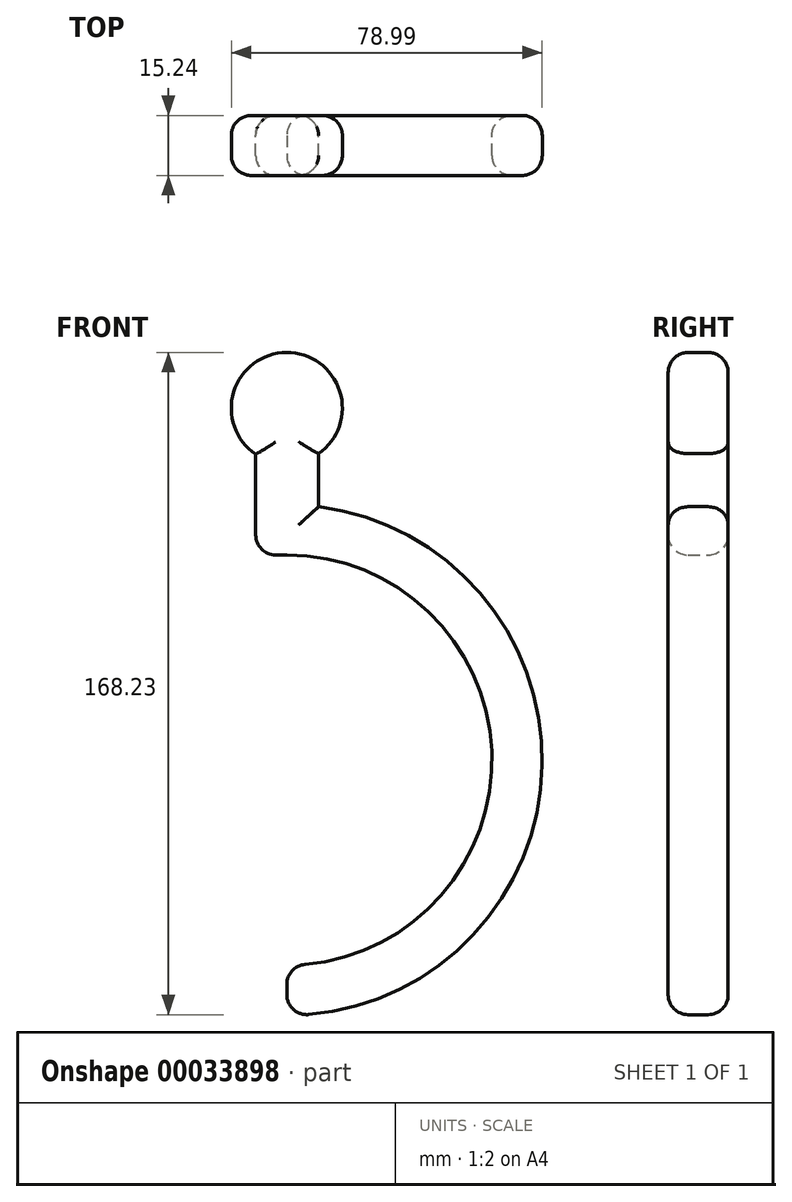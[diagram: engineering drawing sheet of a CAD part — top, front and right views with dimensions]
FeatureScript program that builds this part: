
annotation { "Feature Type Name" : "Feature", "Feature Type Description" : "" }
export const myFeature = defineFeature(function(context is Context, id is Id, definition is map)
    precondition{}
    {
        {
            var Q0;
            Q0=qCreatedBy(makeId("Front.planeOp"),FACE);
            var sketch = newSketch(context, id + "F0", { "sketchPlane" : qUnion([Q0])});
            skArc(sketch, "E0", {"start": v(0, -64.88) * mm, "mid": v(64.88, 0) * mm, "end": v(0, 64.88) * mm});
            skArc(sketch, "E1", {"start": v(0, -52.11) * mm, "mid": v(52.11, 0) * mm, "end": v(0, 52.11) * mm});
            skPoint(sketch, "E2", {"position": v(0, 64.88) * mm});
            skPoint(sketch, "E3", {"position": v(0, 52.11) * mm});
            skPoint(sketch, "E4", {"position": v(0, -52.11) * mm});
            skPoint(sketch, "E5", {"position": v(0, -64.88) * mm});
            skLineSegment(sketch, "E6", {"start": v(0, 64.88) * mm, "end": v(0, 52.11) * mm});
            skLineSegment(sketch, "E7", {"start": v(0, -52.11) * mm, "end": v(0, -64.88) * mm});
            skLineSegment(sketch, "E8.bottom", {"start": v(0, 64.88) * mm, "end": v(-7.9, 64.88) * mm});
            skLineSegment(sketch, "E8.top", {"start": v(0, 89.45) * mm, "end": v(-7.9, 89.45) * mm});
            skLineSegment(sketch, "E8.left", {"start": v(0, 64.88) * mm, "end": v(0, 89.45) * mm});
            skLineSegment(sketch, "E8.right", {"start": v(-7.9, 64.88) * mm, "end": v(-7.9, 89.45) * mm});
            skLineSegment(sketch, "E9.top", {"start": v(0, 52.11) * mm, "end": v(-7.9, 52.11) * mm});
            skLineSegment(sketch, "E9.right", {"start": v(-7.9, 64.88) * mm, "end": v(-7.9, 52.11) * mm});
            skLineSegment(sketch, "E10.bottom", {"start": v(0, 89.45) * mm, "end": v(8.08, 89.45) * mm});
            skLineSegment(sketch, "E10.top", {"start": v(0, 64.38) * mm, "end": v(8.08, 64.38) * mm});
            skLineSegment(sketch, "E10.left", {"start": v(0, 89.45) * mm, "end": v(0, 64.38) * mm});
            skLineSegment(sketch, "E10.right", {"start": v(8.08, 89.45) * mm, "end": v(8.08, 64.38) * mm});
            skCircle(sketch, "E11", {"center": v(0, 89.45) * mm, "radius": 14.11 * mm});
            skSolve(sketch);
        }
        {
            var Q0;
            Q0 = qSketchRegion(id + "F0", true);
            extrude(context, id + "F1", {"entities" : qUnion([Q0]), "depth" : 7.62 * mm, "hasSecondDirection" : true, "secondDirectionOppositeDirection" : true, "secondDirectionDepth" : 7.62 * mm});
        }
        {
            var Q0;
            Q0=makeQuery(id+"F1.opExtrude","CAP_EDGE",EDGE,{"disambiguationData":[OSD([sQuery(id+"F0.wireOp",EDGE,"E0")])],"isStart":false});
            var Q1;
            Q1=makeQuery(id+"F1.opExtrude","CAP_EDGE",EDGE,{"disambiguationData":[OSD([sQuery(id+"F0.wireOp",EDGE,"E0")])],"isStart":true});
            var Q2;
            Q2=makeQuery(id+"F1.opExtrude","CAP_EDGE",EDGE,{"disambiguationData":[OSD([sQuery(id+"F0.wireOp",EDGE,"E10.right")])],"isStart":false});
            var Q3;
            Q3=makeQuery(id+"F1.opExtrude","CAP_EDGE",EDGE,{"disambiguationData":[OSD([sQuery(id+"F0.wireOp",EDGE,"E10.right")])],"isStart":true});
            var Q4;
            Q4=makeQuery(id+"F1.opExtrude","CAP_EDGE",EDGE,{"disambiguationData":[OSD([sQuery(id+"F0.wireOp",EDGE,"E11")])],"isStart":false});
            var Q5;
            Q5=makeQuery(id+"F1.opExtrude","CAP_EDGE",EDGE,{"disambiguationData":[OSD([sQuery(id+"F0.wireOp",EDGE,"E11")])],"isStart":true});
            var Q6;
            Q6=makeQuery(id+"F1.opExtrude","CAP_EDGE",EDGE,{"disambiguationData":[OSD([sQuery(id+"F0.wireOp",EDGE,"E8.right"),sQuery(id+"F0.wireOp",EDGE,"E9.right")])],"isStart":false});
            var Q7;
            Q7=makeQuery(id+"F1.opExtrude","CAP_EDGE",EDGE,{"disambiguationData":[OSD([sQuery(id+"F0.wireOp",EDGE,"E1")])],"isStart":false});
            var Q8;
            Q8=makeQuery(id+"F1.opExtrude","SWEPT_EDGE",EDGE,{"disambiguationData":[OSD([sQuery(id+"F0.wireOp",EDGE,"E9.top"),sQuery(id+"F0.wireOp",EDGE,"E9.right")])]});
            var Q9;
            Q9=makeQuery(id+"F1.opExtrude","CAP_EDGE",EDGE,{"disambiguationData":[OSD([sQuery(id+"F0.wireOp",EDGE,"E9.top")])],"isStart":true});
            var Q10;
            Q10=makeQuery(id+"F1.opExtrude","CAP_EDGE",EDGE,{"disambiguationData":[OSD([sQuery(id+"F0.wireOp",EDGE,"E1")])],"isStart":true});
            var Q11;
            Q11=makeQuery(id+"F1.opExtrude","CAP_EDGE",EDGE,{"disambiguationData":[OSD([sQuery(id+"F0.wireOp",EDGE,"E8.right"),sQuery(id+"F0.wireOp",EDGE,"E9.right")])],"isStart":true});
            var Q12;
            Q12=makeQuery(id+"F1.opExtrude","SWEPT_EDGE",EDGE,{"disambiguationData":[OSD([sQuery(id+"F0.wireOp",EDGE,"E0"),sQuery(id+"F0.wireOp",EDGE,"E7")])]});
            var Q13;
            Q13=makeQuery(id+"F1.opExtrude","SWEPT_EDGE",EDGE,{"disambiguationData":[OSD([sQuery(id+"F0.wireOp",EDGE,"E1"),sQuery(id+"F0.wireOp",EDGE,"E7")])]});
            var Q14;
            Q14=makeQuery(id+"F1.opExtrude","CAP_EDGE",EDGE,{"disambiguationData":[OSD([sQuery(id+"F0.wireOp",EDGE,"E7")])],"isStart":false});
            var Q15;
            Q15=makeQuery(id+"F1.opExtrude","CAP_EDGE",EDGE,{"disambiguationData":[OSD([sQuery(id+"F0.wireOp",EDGE,"E7")])],"isStart":true});
            var Q16;
            Q16=makeQuery(id+"F1.opExtrude","CAP_EDGE",EDGE,{"disambiguationData":[OSD([sQuery(id+"F0.wireOp",EDGE,"E9.top")])],"isStart":false});
            fillet(context, id + "F2", {"entities" : qUnion([Q0, Q1, Q2, Q3, Q4, Q5, Q6, Q7, Q8, Q9, Q10, Q11, Q12, Q13, Q14, Q15, Q16]), "radius" : 5.08 * mm, "tangentPropagation" : true, "allowEdgeOverflow" : false});
        }
    });
